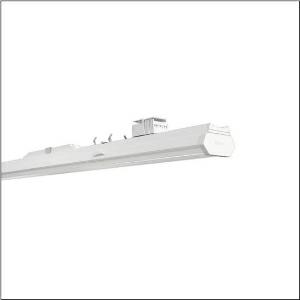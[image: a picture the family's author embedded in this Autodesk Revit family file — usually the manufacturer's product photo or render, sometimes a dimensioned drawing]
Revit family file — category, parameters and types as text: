
# Revit family: licross_r__11_protected_mo_51td1bcn68xg_667e
name_source: partatom
category: Lighting Fixtures
units: mm (PartAtom-declared; Revit-internal decimal feet)

## family parameters
Cut with Voids When Loaded = No
Host = Face
Light Source = No
Part Type = Normal
Room Calculation Point = No
Round Connector Dimension = Use Diameter
Shared = No

## types (1)
- --- (1 x LED, 8310 lm, 49.4 W, 6500K)
    Apparent Load = 49 VA
    CIE Flux Codes = 54 82 95 97 100
    Color Rendering = 80
    Color Temperature = 6500K
    Default Elevation = 1800 mm
    Description = Licross® 11 Protected MO, luminaire insert, of sheet steel, galvanised, coil coated, white, length: 1.500mm, width: 90mm, height: 101mm, LED rated luminous flux: 8.310lm, light colour: 865, control gear: ON/OFF Multilumen, CLOi, with plug, 3-pole, with phase selection, mains connection: 220..240V, AC, 50/60Hz, start of lifetime: 49W, end of service life: 55W, internal wiring halogen-free, primary optical cover: cover, of PMMA, light emission: direct distribution, primary light characteristic: symmetric, protection rating (complete): IP54, insulation class (complete): insulation class I (protective earthing), certification: CE, ENEC, VDE, UKCA, protection symbol: D if used in an environment with non-conductive dust loads with corresponding accessories, impact resistance: IK06, permissible ambient temperature for indoor applications: -35..+40°C, corresponds to IFS (International Featured Standards) requirements for safety and quality in the food industry, reducing of maximum allowable ambient temperature of 5°C with ceiling mounting, LABS conformity tested according to VDMA 24364:2018-05, packaging unit: 1 piece
    Height = 92 mm
    Lamp = 1 x LED
    Lamp Light Flux = 8310 lm
    Lamp Power = 49.4 W
    Lamp count = 1
    Length = 1500 mm
    Luminous efficacy = 168 lm/W
    Manufacturer = Siteco
    ModVariant = No
    Model = 51TD1BCN68XG
    Mounting Place = Ceiling
    Mounting Type = Pendant
    Number of Poles = 1
    OnlyDefault = Yes
    Power Factor = 1
    Product Name = Licross® 11 Protected MO
    Product group = luminaire insert | ceiling pendant
    ProductGroupID = 902
    Protection Class = Protection class I
    Protection Degree = IP 54
    RLX_Detail_Level = 1
    RLX_Emergency_Light_Flux = 0 lm
    RLX_Emergency_Type = 0
    RLX_Emergency_Type_DB = No
    RlxData = <blob elided: 22157 chars, md5=3958ec74>
    Socket = socket
    Standby Power = 0 W
    System Light Flux = 8310 lm
    System Power = 49 W
    Type Comments = factory setting: luminous flux: 100 % | (A | C | E) | 113 mA
    Type Image = l_1256145.jpg
    URL = http://relux.com
    VarID = @adj_041149
    Voltage = 0 V
    Weight = 0.00 kg
    Width = 88 mm

## geometry (parser evidence)
native form markers: Blend x4, Sweep x9
no freeform markers — native parametric forms only
